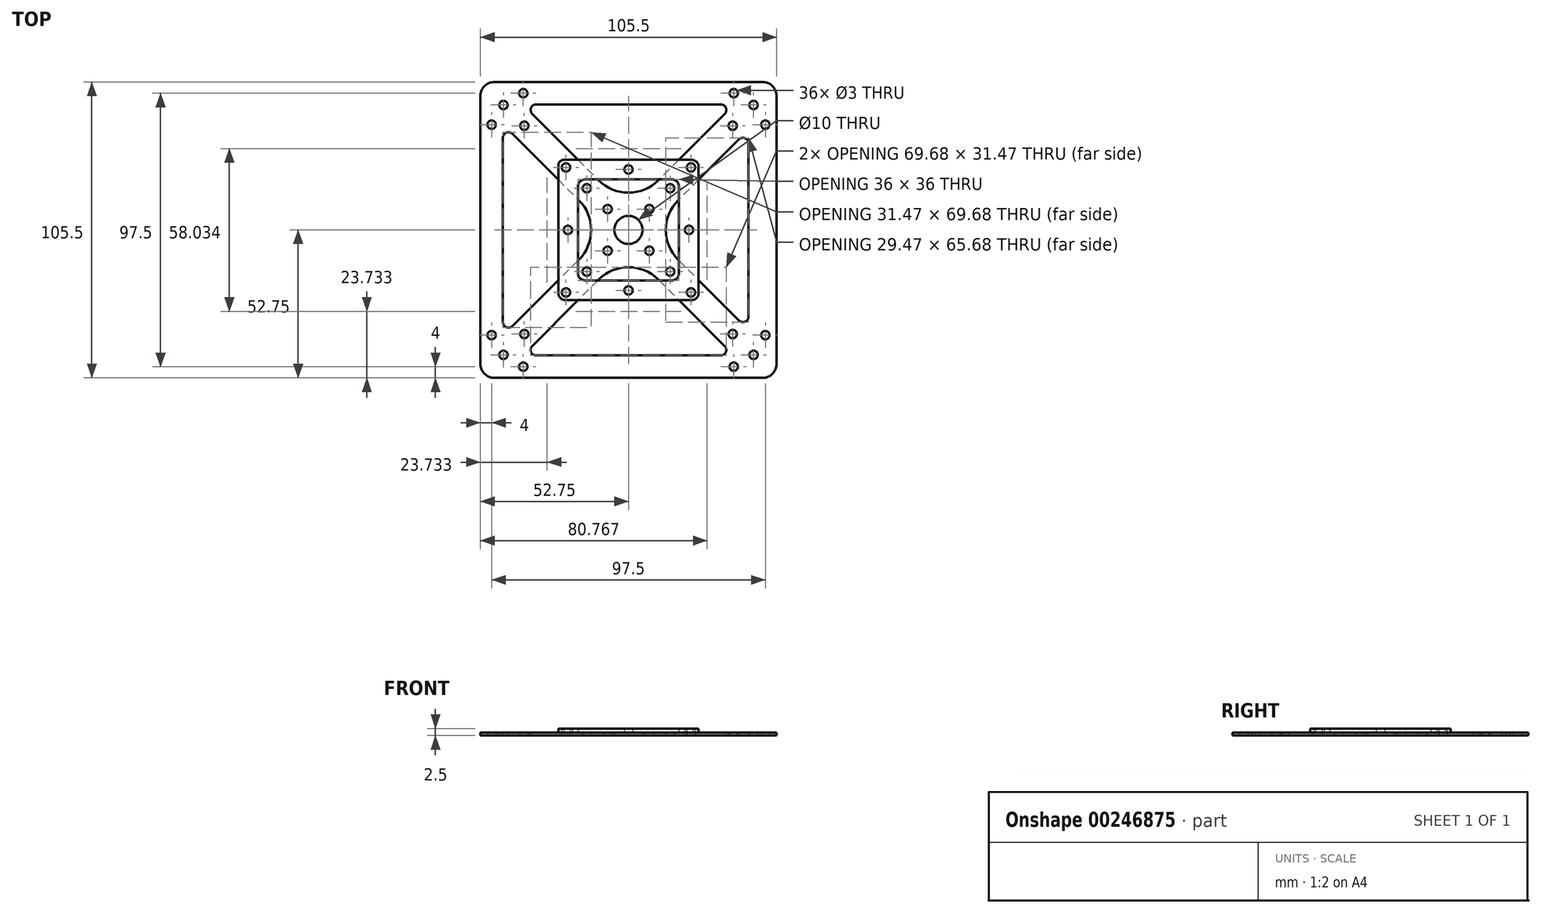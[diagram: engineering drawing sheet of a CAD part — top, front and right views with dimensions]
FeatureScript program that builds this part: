
annotation { "Feature Type Name" : "Feature", "Feature Type Description" : "" }
export const myFeature = defineFeature(function(context is Context, id is Id, definition is map)
    precondition{}
    {
        {
            var Q0;
            Q0=qCreatedBy(makeId("Top.planeOp"),FACE);
            var sketch = newSketch(context, id + "F0", { "sketchPlane" : qUnion([Q0])});
            skLineSegment(sketch, "E0.bottom", {"start": v(-47.75, 52.75) * mm, "end": v(47.75, 52.75) * mm});
            skLineSegment(sketch, "E0.top", {"start": v(-47.75, -52.75) * mm, "end": v(47.75, -52.75) * mm});
            skLineSegment(sketch, "E0.left", {"start": v(-52.75, 47.75) * mm, "end": v(-52.75, -47.75) * mm});
            skLineSegment(sketch, "E0.right", {"start": v(52.75, 47.75) * mm, "end": v(52.75, -47.75) * mm});
            skPoint(sketch, "E0.middle", {"position": v(0, 0) * mm});
            skLineSegment(sketch, "E1.bottom", {"start": v(-32.85, 44.75) * mm, "end": v(32.85, 44.75) * mm});
            skLineSegment(sketch, "E1.top", {"start": v(-32.85, -44.75) * mm, "end": v(32.85, -44.75) * mm});
            skLineSegment(sketch, "E1.left", {"start": v(-44.75, 32.85) * mm, "end": v(-44.75, -32.85) * mm});
            skLineSegment(sketch, "E1.right", {"start": v(42.75, 30.85) * mm, "end": v(42.75, -30.85) * mm});
            skLineSegment(sketch, "E2", {"start": v(-52.75, 52.75) * mm, "end": v(52.75, -52.75) * mm, "construction": true});
            skLineSegment(sketch, "E3", {"start": v(52.75, 52.75) * mm, "end": v(-52.75, -52.75) * mm, "construction": true});
            skLineSegment(sketch, "E4", {"start": v(-34.26, 41.34) * mm, "end": v(-10.6, 17.68) * mm});
            skLineSegment(sketch, "E5", {"start": v(-41.34, 34.26) * mm, "end": v(-17.68, 10.6) * mm});
            skLineSegment(sketch, "E6", {"start": v(34.26, 41.34) * mm, "end": v(10.6, 17.68) * mm});
            skLineSegment(sketch, "E7", {"start": v(39.34, 32.26) * mm, "end": v(17.68, 10.6) * mm});
            skPoint(sketch, "E8.newPointB", {"position": v(-44.75, 44.75) * mm});
            skArc(sketch, "E8.filletArc", {"start": v(-32.85, 44.75) * mm, "mid": v(-34.7, 43.52) * mm, "end": v(-34.26, 41.34) * mm});
            skPoint(sketch, "E9.newPointB", {"position": v(44.75, 44.75) * mm});
            skArc(sketch, "E9.filletArc", {"start": v(34.26, 41.34) * mm, "mid": v(34.7, 43.52) * mm, "end": v(32.85, 44.75) * mm});
            skArc(sketch, "E10.filletArc", {"start": v(-41.34, 34.26) * mm, "mid": v(-43.52, 34.7) * mm, "end": v(-44.75, 32.85) * mm});
            skArc(sketch, "E11.filletArc", {"start": v(-44.75, -32.85) * mm, "mid": v(-43.52, -34.7) * mm, "end": v(-41.34, -34.26) * mm});
            skPoint(sketch, "E12.newPointA", {"position": v(-44.75, -44.75) * mm});
            skArc(sketch, "E12.filletArc", {"start": v(-34.26, -41.34) * mm, "mid": v(-34.7, -43.52) * mm, "end": v(-32.85, -44.75) * mm});
            skPoint(sketch, "E13.newPointA", {"position": v(44.75, -44.75) * mm});
            skArc(sketch, "E13.filletArc", {"start": v(32.85, -44.75) * mm, "mid": v(34.7, -43.52) * mm, "end": v(34.26, -41.34) * mm});
            skArc(sketch, "E14.filletArc", {"start": v(39.34, -32.26) * mm, "mid": v(41.52, -32.7) * mm, "end": v(42.75, -30.85) * mm});
            skArc(sketch, "E15.filletArc", {"start": v(42.75, 30.85) * mm, "mid": v(41.52, 32.7) * mm, "end": v(39.34, 32.26) * mm});
            skLineSegment(sketch, "E16.trimOffspring", {"start": v(-17.68, -10.6) * mm, "end": v(-41.34, -34.26) * mm});
            skLineSegment(sketch, "E17.trimOffspring", {"start": v(10.6, -17.68) * mm, "end": v(34.26, -41.34) * mm});
            skLineSegment(sketch, "E18.trimOffspring", {"start": v(-10.6, -17.68) * mm, "end": v(-34.26, -41.34) * mm});
            skLineSegment(sketch, "E19.trimOffspring", {"start": v(17.68, -10.6) * mm, "end": v(39.34, -32.26) * mm});
            skPoint(sketch, "E20.visualSharp", {"position": v(-7.07, 0) * mm});
            skArc(sketch, "E20.filletArc", {"start": v(-17.68, -10.6) * mm, "mid": v(-13.28, 0) * mm, "end": v(-17.68, 10.6) * mm});
            skPoint(sketch, "E21.visualSharp", {"position": v(0, 7.07) * mm});
            skArc(sketch, "E21.filletArc", {"start": v(-10.6, 17.68) * mm, "mid": v(0, 13.28) * mm, "end": v(10.6, 17.68) * mm});
            skPoint(sketch, "E22.visualSharp", {"position": v(7.07, 0) * mm});
            skArc(sketch, "E22.filletArc", {"start": v(17.68, 10.6) * mm, "mid": v(13.28, 0) * mm, "end": v(17.68, -10.6) * mm});
            skPoint(sketch, "E23.visualSharp", {"position": v(0, -7.07) * mm});
            skArc(sketch, "E23.filletArc", {"start": v(10.6, -17.68) * mm, "mid": v(0, -13.28) * mm, "end": v(-10.6, -17.68) * mm});
            skPoint(sketch, "E24.visualSharp", {"position": v(-52.75, 52.75) * mm});
            skArc(sketch, "E24.filletArc", {"start": v(-47.75, 52.75) * mm, "mid": v(-51.29, 51.29) * mm, "end": v(-52.75, 47.75) * mm});
            skPoint(sketch, "E25.visualSharp", {"position": v(52.75, 52.75) * mm});
            skArc(sketch, "E25.filletArc", {"start": v(52.75, 47.75) * mm, "mid": v(51.29, 51.29) * mm, "end": v(47.75, 52.75) * mm});
            skPoint(sketch, "E26.visualSharp", {"position": v(52.75, -52.75) * mm});
            skArc(sketch, "E26.filletArc", {"start": v(47.75, -52.75) * mm, "mid": v(51.29, -51.29) * mm, "end": v(52.75, -47.75) * mm});
            skPoint(sketch, "E27.visualSharp", {"position": v(-52.75, -52.75) * mm});
            skArc(sketch, "E27.filletArc", {"start": v(-52.75, -47.75) * mm, "mid": v(-51.29, -51.29) * mm, "end": v(-47.75, -52.75) * mm});
            skCircle(sketch, "E28", {"center": v(-44.55, 44.55) * mm, "radius": 1.5 * mm});
            skCircle(sketch, "E29", {"center": v(-37.5, 48.75) * mm, "radius": 1.5 * mm});
            skCircle(sketch, "E30", {"center": v(-48.75, 37.5) * mm, "radius": 1.5 * mm});
            skCircle(sketch, "E31", {"center": v(-37.12, 37.12) * mm, "radius": 1.5 * mm});
            skCircle(sketch, "E32", {"center": v(-22.27, 22.27) * mm, "radius": 1.5 * mm});
            skCircle(sketch, "E33", {"center": v(-14.85, 14.85) * mm, "radius": 1.5 * mm});
            skCircle(sketch, "E34", {"center": v(-7.42, 7.42) * mm, "radius": 1.5 * mm});
            skCircle(sketch, "E35.1.0", {"center": v(-44.55, -44.55) * mm, "radius": 1.5 * mm});
            skCircle(sketch, "E35.1.1", {"center": v(-37.5, -48.75) * mm, "radius": 1.5 * mm});
            skCircle(sketch, "E35.1.2", {"center": v(-37.12, -37.12) * mm, "radius": 1.5 * mm});
            skCircle(sketch, "E35.1.3", {"center": v(-48.75, -37.5) * mm, "radius": 1.5 * mm});
            skCircle(sketch, "E35.1.4", {"center": v(-22.27, -22.27) * mm, "radius": 1.5 * mm});
            skCircle(sketch, "E35.1.5", {"center": v(-14.85, -14.85) * mm, "radius": 1.5 * mm});
            skCircle(sketch, "E35.1.6", {"center": v(-7.42, -7.42) * mm, "radius": 1.5 * mm});
            skCircle(sketch, "E35.2.0", {"center": v(44.55, -44.55) * mm, "radius": 1.5 * mm});
            skCircle(sketch, "E35.2.1", {"center": v(48.75, -37.5) * mm, "radius": 1.5 * mm});
            skCircle(sketch, "E35.2.2", {"center": v(37.12, -37.12) * mm, "radius": 1.5 * mm});
            skCircle(sketch, "E35.2.3", {"center": v(37.5, -48.75) * mm, "radius": 1.5 * mm});
            skCircle(sketch, "E35.2.4", {"center": v(22.27, -22.27) * mm, "radius": 1.5 * mm});
            skCircle(sketch, "E35.2.5", {"center": v(14.85, -14.85) * mm, "radius": 1.5 * mm});
            skCircle(sketch, "E35.2.6", {"center": v(7.42, -7.42) * mm, "radius": 1.5 * mm});
            skCircle(sketch, "E35.3.0", {"center": v(44.55, 44.55) * mm, "radius": 1.5 * mm});
            skCircle(sketch, "E35.3.1", {"center": v(37.5, 48.75) * mm, "radius": 1.5 * mm});
            skCircle(sketch, "E35.3.2", {"center": v(37.12, 37.12) * mm, "radius": 1.5 * mm});
            skCircle(sketch, "E35.3.3", {"center": v(48.75, 37.5) * mm, "radius": 1.5 * mm});
            skCircle(sketch, "E35.3.4", {"center": v(22.27, 22.27) * mm, "radius": 1.5 * mm});
            skCircle(sketch, "E35.3.5", {"center": v(14.85, 14.85) * mm, "radius": 1.5 * mm});
            skCircle(sketch, "E35.3.6", {"center": v(7.42, 7.42) * mm, "radius": 1.5 * mm});
            skCircle(sketch, "E36", {"center": v(0, 0) * mm, "radius": 5 * mm});
            skSolve(sketch);
        }
        {
            var Q0;
            Q0=makeQuery(id+"F0.imprint","IMPRINT",FACE,{"disambiguationData":[TD([[makeQuery(id+"F0.imprint","IMPRINT",EDGE,{"derivedFrom":sQuery(id+"F0.wireOp",EDGE,"E0.bottom")}),-1.0]])]});
            extrude(context, id + "F1", {"entities" : qUnion([Q0]), "depth" : 1 * mm});
        }
        {
            var Q0;
            Q0=makeQuery(id+"F1.opExtrude","CAP_FACE",FACE,{"disambiguationData":[OSD([sQuery(id+"F0.wireOp",EDGE,"E0.bottom"),sQuery(id+"F0.wireOp",EDGE,"E0.top"),sQuery(id+"F0.wireOp",EDGE,"E0.left"),sQuery(id+"F0.wireOp",EDGE,"E0.right"),sQuery(id+"F0.wireOp",EDGE,"E1.bottom"),sQuery(id+"F0.wireOp",EDGE,"E1.top"),sQuery(id+"F0.wireOp",EDGE,"E1.left"),sQuery(id+"F0.wireOp",EDGE,"E1.right"),sQuery(id+"F0.wireOp",EDGE,"E4"),sQuery(id+"F0.wireOp",EDGE,"E5"),sQuery(id+"F0.wireOp",EDGE,"E6"),sQuery(id+"F0.wireOp",EDGE,"E7"),sQuery(id+"F0.wireOp",EDGE,"E8.filletArc"),sQuery(id+"F0.wireOp",EDGE,"E9.filletArc"),sQuery(id+"F0.wireOp",EDGE,"E10.filletArc"),sQuery(id+"F0.wireOp",EDGE,"E11.filletArc"),sQuery(id+"F0.wireOp",EDGE,"E12.filletArc"),sQuery(id+"F0.wireOp",EDGE,"E13.filletArc"),sQuery(id+"F0.wireOp",EDGE,"E14.filletArc"),sQuery(id+"F0.wireOp",EDGE,"E15.filletArc"),sQuery(id+"F0.wireOp",EDGE,"E16.trimOffspring"),sQuery(id+"F0.wireOp",EDGE,"E17.trimOffspring"),sQuery(id+"F0.wireOp",EDGE,"E18.trimOffspring"),sQuery(id+"F0.wireOp",EDGE,"E19.trimOffspring"),sQuery(id+"F0.wireOp",EDGE,"E20.filletArc"),sQuery(id+"F0.wireOp",EDGE,"E21.filletArc"),sQuery(id+"F0.wireOp",EDGE,"E22.filletArc"),sQuery(id+"F0.wireOp",EDGE,"E23.filletArc"),sQuery(id+"F0.wireOp",EDGE,"E24.filletArc"),sQuery(id+"F0.wireOp",EDGE,"E25.filletArc"),sQuery(id+"F0.wireOp",EDGE,"E26.filletArc"),sQuery(id+"F0.wireOp",EDGE,"E27.filletArc"),sQuery(id+"F0.wireOp",EDGE,"E28"),sQuery(id+"F0.wireOp",EDGE,"E29"),sQuery(id+"F0.wireOp",EDGE,"E30"),sQuery(id+"F0.wireOp",EDGE,"E31"),sQuery(id+"F0.wireOp",EDGE,"E32"),sQuery(id+"F0.wireOp",EDGE,"E33"),sQuery(id+"F0.wireOp",EDGE,"E34"),sQuery(id+"F0.wireOp",EDGE,"E35.1.0"),sQuery(id+"F0.wireOp",EDGE,"E35.1.1"),sQuery(id+"F0.wireOp",EDGE,"E35.1.2"),sQuery(id+"F0.wireOp",EDGE,"E35.1.3"),sQuery(id+"F0.wireOp",EDGE,"E35.1.4"),sQuery(id+"F0.wireOp",EDGE,"E35.1.5"),sQuery(id+"F0.wireOp",EDGE,"E35.1.6"),sQuery(id+"F0.wireOp",EDGE,"E35.2.0"),sQuery(id+"F0.wireOp",EDGE,"E35.2.1"),sQuery(id+"F0.wireOp",EDGE,"E35.2.2"),sQuery(id+"F0.wireOp",EDGE,"E35.2.3"),sQuery(id+"F0.wireOp",EDGE,"E35.2.4"),sQuery(id+"F0.wireOp",EDGE,"E35.2.5"),sQuery(id+"F0.wireOp",EDGE,"E35.2.6"),sQuery(id+"F0.wireOp",EDGE,"E35.3.0"),sQuery(id+"F0.wireOp",EDGE,"E35.3.1"),sQuery(id+"F0.wireOp",EDGE,"E35.3.2"),sQuery(id+"F0.wireOp",EDGE,"E35.3.3"),sQuery(id+"F0.wireOp",EDGE,"E35.3.4"),sQuery(id+"F0.wireOp",EDGE,"E35.3.5"),sQuery(id+"F0.wireOp",EDGE,"E35.3.6"),sQuery(id+"F0.wireOp",EDGE,"E36")])],"isStart":false});
            var sketch = newSketch(context, id + "F2", { "sketchPlane" : qUnion([Q0])});
            skCircle(sketch, "E37.0", {"center": v(-22.27, 22.27) * mm, "radius": 1.5 * mm});
            skCircle(sketch, "E38.0", {"center": v(22.27, 22.27) * mm, "radius": 1.5 * mm});
            skCircle(sketch, "E39.0", {"center": v(-22.27, -22.27) * mm, "radius": 1.5 * mm});
            skCircle(sketch, "E40.0", {"center": v(22.27, -22.27) * mm, "radius": 1.5 * mm});
            skCircle(sketch, "E41", {"center": v(0, 21.57) * mm, "radius": 1.5 * mm});
            skCircle(sketch, "E42.1.0", {"center": v(-21.57, 0) * mm, "radius": 1.5 * mm});
            skCircle(sketch, "E42.2.0", {"center": v(0, -21.57) * mm, "radius": 1.5 * mm});
            skCircle(sketch, "E42.3.0", {"center": v(21.57, 0) * mm, "radius": 1.5 * mm});
            skPoint(sketch, "E42.center", {"position": v(0, 0) * mm});
            skLineSegment(sketch, "E43.bottom", {"start": v(-23, 25) * mm, "end": v(22.5, 25) * mm});
            skLineSegment(sketch, "E43.top", {"start": v(-22.5, -25) * mm, "end": v(22.5, -25) * mm});
            skLineSegment(sketch, "E43.left", {"start": v(-25, 23) * mm, "end": v(-25, -22.5) * mm});
            skLineSegment(sketch, "E43.right", {"start": v(25, 22.5) * mm, "end": v(25, -22.5) * mm});
            skPoint(sketch, "E44.visualSharp", {"position": v(-25, 25) * mm});
            skArc(sketch, "E44.filletArc", {"start": v(-23, 25) * mm, "mid": v(-24.41, 24.41) * mm, "end": v(-25, 23) * mm});
            skPoint(sketch, "E45.visualSharp", {"position": v(25, 25) * mm});
            skArc(sketch, "E45.filletArc", {"start": v(25, 22.5) * mm, "mid": v(24.27, 24.27) * mm, "end": v(22.5, 25) * mm});
            skPoint(sketch, "E46.visualSharp", {"position": v(-25, -25) * mm});
            skArc(sketch, "E46.filletArc", {"start": v(-25, -22.5) * mm, "mid": v(-24.27, -24.27) * mm, "end": v(-22.5, -25) * mm});
            skPoint(sketch, "E47.visualSharp", {"position": v(25, -25) * mm});
            skArc(sketch, "E47.filletArc", {"start": v(22.5, -25) * mm, "mid": v(24.27, -24.27) * mm, "end": v(25, -22.5) * mm});
            skLineSegment(sketch, "E48.bottom", {"start": v(-15.5, 18) * mm, "end": v(15.5, 18) * mm});
            skLineSegment(sketch, "E48.top", {"start": v(-15.5, -18) * mm, "end": v(15.5, -18) * mm});
            skLineSegment(sketch, "E48.left", {"start": v(-18, 15.5) * mm, "end": v(-18, -15.5) * mm});
            skLineSegment(sketch, "E48.right", {"start": v(18, 15.5) * mm, "end": v(18, -15.5) * mm});
            skPoint(sketch, "E49.visualSharp", {"position": v(-18, 18) * mm});
            skArc(sketch, "E49.filletArc", {"start": v(-15.5, 18) * mm, "mid": v(-17.27, 17.27) * mm, "end": v(-18, 15.5) * mm});
            skPoint(sketch, "E50.visualSharp", {"position": v(18, 18) * mm});
            skArc(sketch, "E50.filletArc", {"start": v(18, 15.5) * mm, "mid": v(17.27, 17.27) * mm, "end": v(15.5, 18) * mm});
            skPoint(sketch, "E51.visualSharp", {"position": v(18, -18) * mm});
            skArc(sketch, "E51.filletArc", {"start": v(15.5, -18) * mm, "mid": v(17.27, -17.27) * mm, "end": v(18, -15.5) * mm});
            skPoint(sketch, "E52.visualSharp", {"position": v(-18, -18) * mm});
            skArc(sketch, "E52.filletArc", {"start": v(-18, -15.5) * mm, "mid": v(-17.27, -17.27) * mm, "end": v(-15.5, -18) * mm});
            skSolve(sketch);
        }
        {
            var Q0;
            Q0=makeQuery(id+"F2.imprint","IMPRINT",FACE,{"disambiguationData":[TD([[makeQuery(id+"F2.imprint","IMPRINT",EDGE,{"derivedFrom":sQuery(id+"F2.wireOp",EDGE,"E37.0")}),-1.0]])]});
            var Q1;
            Q1=makeQuery(id+"F2.imprint","IMPRINT",FACE,{"disambiguationData":[TD([[makeQuery(id+"F2.imprint","IMPRINT",EDGE,{"derivedFrom":sQuery(id+"F2.wireOp",EDGE,"E41")}),-1.0]])]});
            var Q2;
            Q2=makeQuery(id+"F2.imprint","IMPRINT",FACE,{"disambiguationData":[TD([[makeQuery(id+"F2.imprint","IMPRINT",EDGE,{"derivedFrom":sQuery(id+"F2.wireOp",EDGE,"E38.0")}),-1.0]])]});
            var Q3;
            Q3=makeQuery(id+"F2.imprint","IMPRINT",FACE,{"disambiguationData":[TD([[makeQuery(id+"F2.imprint","IMPRINT",EDGE,{"derivedFrom":sQuery(id+"F2.wireOp",EDGE,"E42.3.0")}),-1.0]])]});
            var Q4;
            Q4=makeQuery(id+"F2.imprint","IMPRINT",FACE,{"disambiguationData":[TD([[makeQuery(id+"F2.imprint","IMPRINT",EDGE,{"derivedFrom":sQuery(id+"F2.wireOp",EDGE,"E40.0")}),-1.0]])]});
            var Q5;
            Q5=makeQuery(id+"F2.imprint","IMPRINT",FACE,{"disambiguationData":[TD([[makeQuery(id+"F2.imprint","IMPRINT",EDGE,{"derivedFrom":sQuery(id+"F2.wireOp",EDGE,"E42.1.0")}),-1.0]])]});
            var Q6;
            Q6=makeQuery(id+"F2.imprint","IMPRINT",FACE,{"disambiguationData":[TD([[makeQuery(id+"F2.imprint","IMPRINT",EDGE,{"derivedFrom":sQuery(id+"F2.wireOp",EDGE,"E39.0")}),-1.0]])]});
            var Q7;
            Q7=makeQuery(id+"F2.imprint","IMPRINT",FACE,{"disambiguationData":[TD([[makeQuery(id+"F2.imprint","IMPRINT",EDGE,{"derivedFrom":sQuery(id+"F2.wireOp",EDGE,"E42.2.0")}),-1.0]])]});
            extrude(context, id + "F3", {"entities" : qUnion([Q0, Q1, Q2, Q3, Q4, Q5, Q6, Q7]), "depth" : 1.5 * mm});
        }
    });
